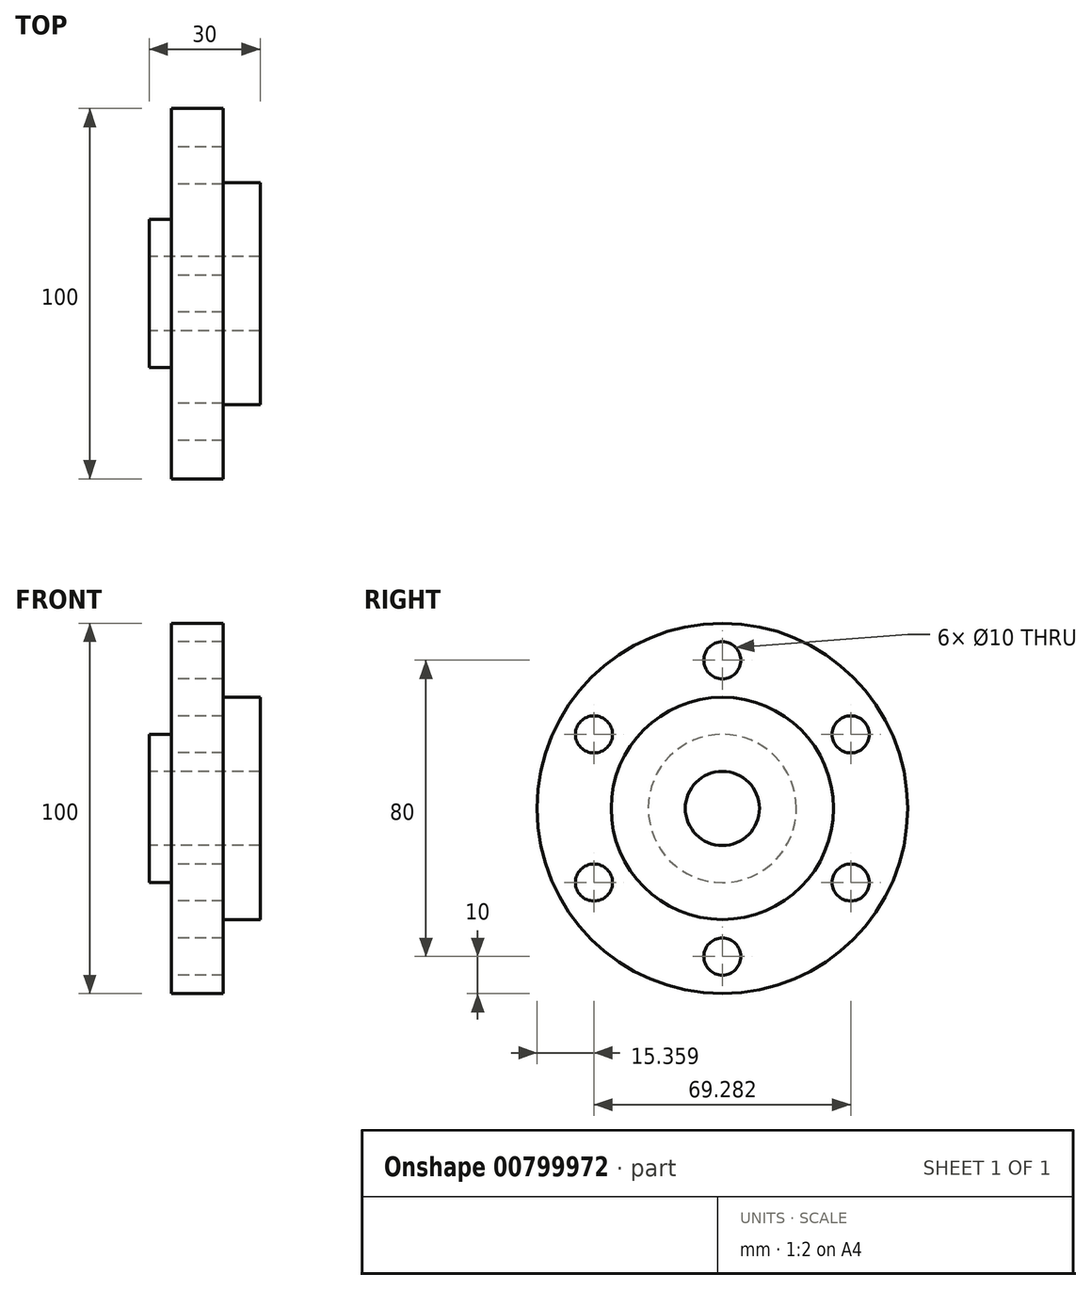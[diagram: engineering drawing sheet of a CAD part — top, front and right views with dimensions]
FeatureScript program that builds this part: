
annotation { "Feature Type Name" : "Feature", "Feature Type Description" : "" }
export const myFeature = defineFeature(function(context is Context, id is Id, definition is map)
    precondition{}
    {
        {
            var Q0;
            Q0=qCreatedBy(makeId("Front.planeOp"),FACE);
            var sketch = newSketch(context, id + "F0", { "sketchPlane" : qUnion([Q0])});
            skLineSegment(sketch, "E0", {"start": v(-111.86, 0) * mm, "end": v(119.49, 0) * mm, "construction": true});
            skLineSegment(sketch, "E1", {"start": v(0, 10) * mm, "end": v(30, 10) * mm});
            skLineSegment(sketch, "E2", {"start": v(30, 10) * mm, "end": v(30, 30) * mm});
            skLineSegment(sketch, "E3", {"start": v(30, 30) * mm, "end": v(20, 30) * mm});
            skLineSegment(sketch, "E4", {"start": v(20, 30) * mm, "end": v(20, 50) * mm});
            skLineSegment(sketch, "E5", {"start": v(20, 50) * mm, "end": v(6, 50) * mm});
            skLineSegment(sketch, "E6", {"start": v(6, 50) * mm, "end": v(6, 20) * mm});
            skLineSegment(sketch, "E7", {"start": v(6, 20) * mm, "end": v(0, 20) * mm});
            skLineSegment(sketch, "E8", {"start": v(0, 20) * mm, "end": v(0, 10) * mm});
            skSolve(sketch);
        }
        {
            var Q0;
            Q0 = qSketchRegion(id + "F0", true);
            var Q1;
            Q1=sQuery(id+"F0.wireOp",EDGE,"E0");
            revolve(context, id + "F1", {"surfaceOperationType" : NewSurfaceOperationType.NEW, "entities" : qUnion([Q0]), "axis" : qUnion([Q1]), "revolveType" : RevolveType.FULL});
        }
        {
            var Q0;
            Q0=qCreatedBy(makeId("Right.planeOp"),FACE);
            var sketch = newSketch(context, id + "F2", { "sketchPlane" : qUnion([Q0])});
            skCircle(sketch, "E9", {"center": v(0, 0) * mm, "radius": 40 * mm, "construction": true});
            skCircle(sketch, "E10", {"center": v(0, 40) * mm, "radius": 5 * mm});
            skCircle(sketch, "E11.1.0", {"center": v(-34.64, 20) * mm, "radius": 5 * mm});
            skCircle(sketch, "E11.2.0", {"center": v(-34.64, -20) * mm, "radius": 5 * mm});
            skCircle(sketch, "E11.3.0", {"center": v(0, -40) * mm, "radius": 5 * mm});
            skCircle(sketch, "E11.4.0", {"center": v(34.64, -20) * mm, "radius": 5 * mm});
            skCircle(sketch, "E11.5.0", {"center": v(34.64, 20) * mm, "radius": 5 * mm});
            skSolve(sketch);
        }
        {
            var Q0;
            Q0 = qSketchRegion(id + "F2", true);
            extrude(context, id + "F3", {"entities" : qUnion([Q0]), "operationType" : NewBodyOperationType.REMOVE, "endBound" : BoundingType.THROUGH_ALL, "depth" : 25 * mm, "offsetDistance" : 25 * mm});
        }
    });
